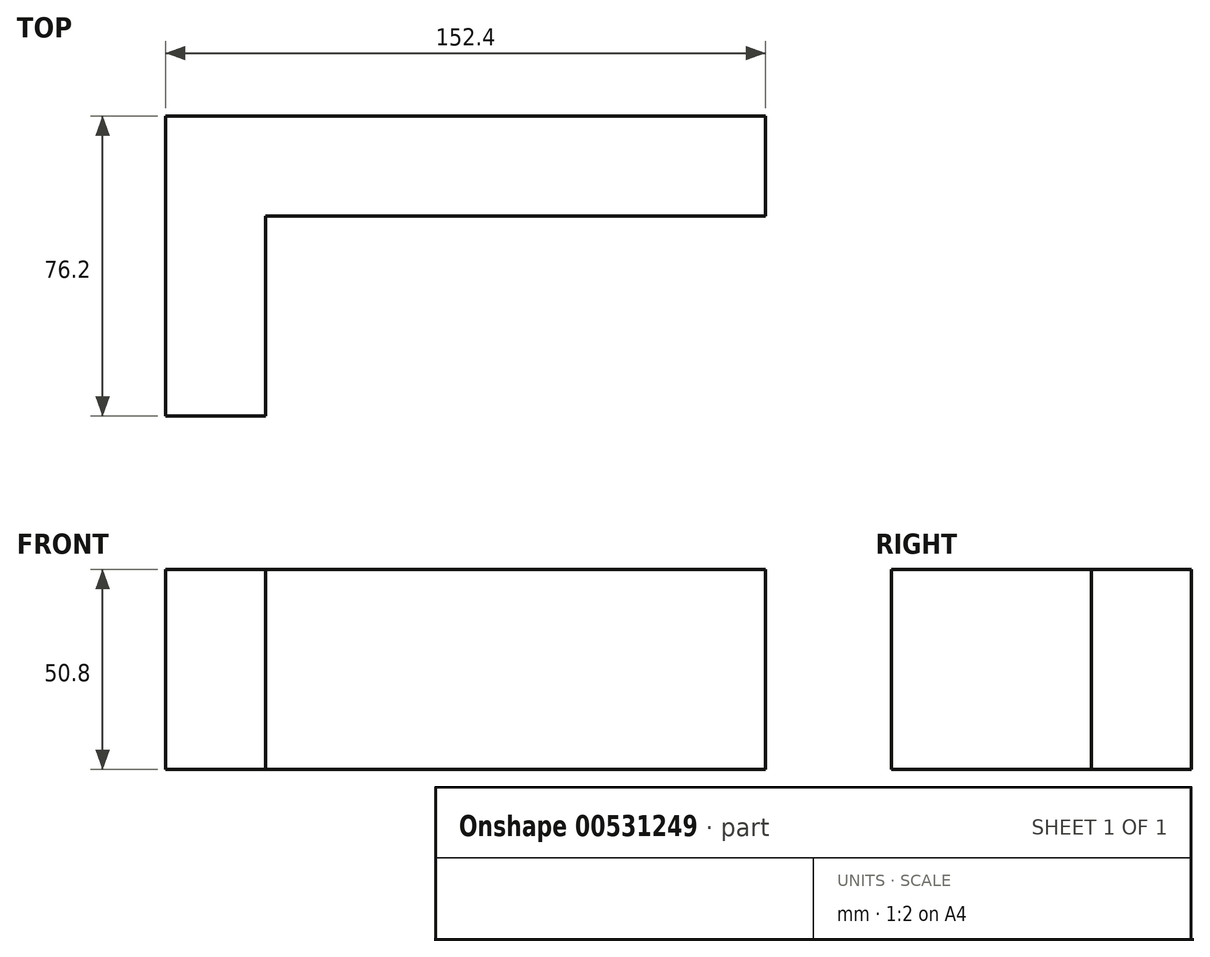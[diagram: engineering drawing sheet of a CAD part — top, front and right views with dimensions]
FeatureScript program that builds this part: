
annotation { "Feature Type Name" : "Feature", "Feature Type Description" : "" }
export const myFeature = defineFeature(function(context is Context, id is Id, definition is map)
    precondition{}
    {
        {
            var Q0;
            Q0=qCreatedBy(makeId("Top.planeOp"),FACE);
            var sketch = newSketch(context, id + "F0", { "sketchPlane" : qUnion([Q0])});
            skLineSegment(sketch, "E0", {"start": v(-62.11, 42.88) * mm, "end": v(-62.11, -33.32) * mm});
            skLineSegment(sketch, "E1", {"start": v(-62.11, -33.32) * mm, "end": v(-36.71, -33.32) * mm});
            skLineSegment(sketch, "E2", {"start": v(-36.71, -33.32) * mm, "end": v(-36.71, 17.48) * mm});
            skLineSegment(sketch, "E3", {"start": v(90.29, 42.88) * mm, "end": v(-62.11, 42.88) * mm});
            skLineSegment(sketch, "E4", {"start": v(-36.71, 17.48) * mm, "end": v(90.29, 17.48) * mm});
            skLineSegment(sketch, "E5", {"start": v(90.29, 17.48) * mm, "end": v(90.29, 42.88) * mm});
            skSolve(sketch);
        }
        {
            var Q0;
            Q0=qCreatedBy(makeId("Top.planeOp"),FACE);
            var sketch = newSketch(context, id + "F1", { "sketchPlane" : qUnion([Q0])});
            skLineSegment(sketch, "E6.bottom", {"start": v(90.29, 42.88) * mm, "end": v(39.49, 42.88) * mm});
            skLineSegment(sketch, "E6.top", {"start": v(90.29, 17.48) * mm, "end": v(39.49, 17.48) * mm});
            skLineSegment(sketch, "E6.left", {"start": v(90.29, 42.88) * mm, "end": v(90.29, 17.48) * mm});
            skLineSegment(sketch, "E6.right", {"start": v(39.49, 42.88) * mm, "end": v(39.49, 17.48) * mm});
            skSolve(sketch);
        }
        {
            var Q0;
            Q0 = qSketchRegion(id + "F1", true);
            extrude(context, id + "F2", {"entities" : qUnion([Q0]), "depth" : 25.4 * mm, "offsetDistance" : 25.4 * mm});
        }
        {
            var Q0;
            Q0=makeQuery(id+"F0.imprint","IMPRINT",FACE,{"disambiguationData":[TD([[makeQuery(id+"F0.imprint","IMPRINT",EDGE,{"derivedFrom":sQuery(id+"F0.wireOp",EDGE,"E0")}),1.0]])]});
            extrude(context, id + "F3", {"entities" : qUnion([Q0]), "operationType" : NewBodyOperationType.ADD, "depth" : 50.8 * mm, "offsetDistance" : 25.4 * mm});
        }
    });
